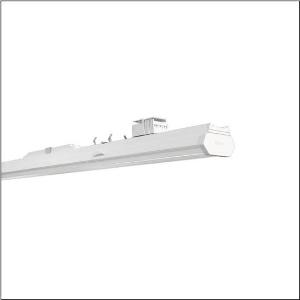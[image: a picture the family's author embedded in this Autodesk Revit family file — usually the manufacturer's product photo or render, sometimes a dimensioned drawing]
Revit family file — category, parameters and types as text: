
# Revit family: licross_21_protected_ho_52td12dn4axm
name_source: partatom
category: Lighting Fixtures
units: mm (PartAtom-declared; Revit-internal decimal feet)

## family parameters
Cut with Voids When Loaded = No
Host = Face
Light Source = No
Part Type = Normal
Room Calculation Point = No
Round Connector Dimension = Use Diameter
Shared = No

## types (1)
- --- (1 x LED, 10000 lm, 56 W, 4000K)
    Apparent Load = 56 VA
    CIE Flux Codes = 70 91 97 98 100
    Color Rendering = 80
    Color Temperature = 4000K
    Default Elevation = 1800 mm
    Description = Licross 21 Protected HO, luminaire insert, of sheet steel, galvanised, coil coated, white, length: 1.500mm, width: 90mm, height: 103mm, LED rated luminous flux: 10.000lm, light colour: 840, SDCM (Standard Deviation of Colour Matching)MacAdam ≤ 3 SDCM (initial), control gear: DALI 2, with plug, 5-pole, with phase selection, mains connection: 220..240V, AC, 50/60Hz, rated input power: 56W, internal wiring halogen-free, primary light control with lens, of plastic, primary optical cover: cover, of PMMA, light emission: direct distribution, primary light characteristic: symmetric, protection rating (complete): IP54, insulation class (complete): insulation class I (protective earthing), certification: CE, ENEC, VDE, UKCA, protection symbol: D if used in an environment with non-conductive dust loads with corresponding accessories, impact resistance: IK06, permissible ambient temperature for indoor applications: -25..+45°C, corresponds to IFS (International Featured Standards) requirements for safety and quality in the food industry, reducing of maximum allowable ambient temperature of 5°C with ceiling mounting, LABS conformity tested according to VDMA 24364:2018-05, The light source and the operating device comply with the requirements of the Ecodesign Regulation (EU) 2019/2020 and are replaceable in accordance with this regulation, packaging unit: 1 piece
    Height = 92 mm
    Lamp = 1 x LED
    Lamp Light Flux = 10000 lm
    Lamp Power = 56 W
    Lamp count = 1
    Length = 1500 mm
    Luminous efficacy = 179 lm/W
    Manufacturer = Siteco
    ModVariant = No
    Model = 52TD12DN4AXM
    Mounting Place = Ceiling
    Mounting Type = Pendant
    Number of Poles = 1
    OnlyDefault = Yes
    Power Factor = 1
    Product Name = Licross 21 Protected HO
    Product group = luminaire insert | ceiling pendant
    ProductGroupID = 901
    Protection Class = Protection class I
    Protection Degree = IP 54
    RLX_Detail_Level = 1
    RLX_Emergency_Light_Flux = 0 lm
    RLX_Emergency_Type = 0
    RLX_Emergency_Type_DB = No
    RlxData = <blob elided: 24593 chars, md5=c19f6845>
    Socket = socket
    Standby Power = 0 W
    System Light Flux = 10000 lm
    System Power = 56 W
    Type Comments = factory setting: luminous flux: 100 % | dim-lin: 254 | 321 mA
    Type Image = l_1256148.jpg
    URL = http://relux.com
    VarID = @adj_130693
    Voltage = 0 V
    Weight = 0.00 kg
    Width = 88 mm

## geometry (parser evidence)
native form markers: Blend x4, Sweep x10
no freeform markers — native parametric forms only
